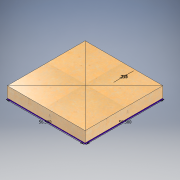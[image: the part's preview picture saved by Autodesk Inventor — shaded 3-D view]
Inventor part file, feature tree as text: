
AUTODESK INVENTOR PART (.ipt)
format: ipt  version: 2022.2 (Build 262287010, 287A)  size: 184,320 bytes
history: native  units: in
note: dims shown in document units (in); Inventor stores cm internally (conversion verified against a paired STEP export)
features: extrude x5, sketch x3, projected_geometry x2
ambient origin geometry x8: Origin, YZ Plane, XZ Plane, XY Plane, X Axis, Y Axis, Z Axis, Center Point
bodies: Solid1 (feature_tree)
feature tree (10):
  sketch  "Sketch1"  dims[d0=56.5in d1=56.5in]
  extrude  "Extrusion1"  Depth=56.5in
  sketch  "Sketch2"  dims[d2=0.375in d3=0.25in]
  sketch  "Sketch3"  dims[d4=8.5in d5=0.0in d6=0.25in d7=0.25in d8=0.25in d9=0.25in d10=0.0in d11=0.0in d12=0.0in d13=0.0in d14=0.75in d15=0.0in d16=0.5in d17=0.0in]
  extrude  "Extrusion2"  Depth=0.25in
  extrude  "Extrusion3"  Depth=0.25in
  extrude  "Extrusion4"  Depth=0.25in
  extrude  "Extrusion5"  Depth=0.25in
  projected_geometry  "Projected Loop1"
  projected_geometry  "Projected Loop2"
